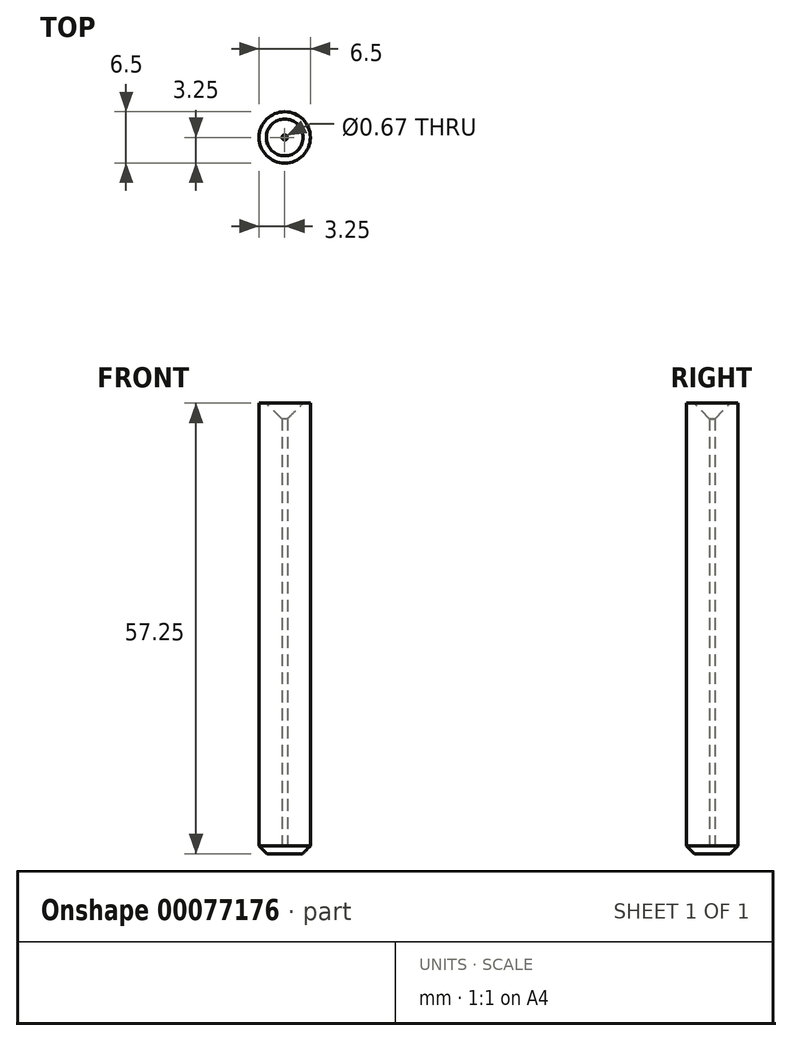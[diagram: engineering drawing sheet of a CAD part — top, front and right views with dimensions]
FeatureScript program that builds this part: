
annotation { "Feature Type Name" : "Feature", "Feature Type Description" : "" }
export const myFeature = defineFeature(function(context is Context, id is Id, definition is map)
    precondition{}
    {
        {
            var Q0;
            Q0=qCreatedBy(makeId("Top.planeOp"),FACE);
            var sketch = newSketch(context, id + "F0", { "sketchPlane" : qUnion([Q0])});
            skCircle(sketch, "E0", {"center": v(0, 0) * mm, "radius": 3.25 * mm});
            skCircle(sketch, "E1", {"center": v(0, 0) * mm, "radius": 0.34 * mm});
            skSolve(sketch);
        }
        {
            var Q0;
            Q0=qSketchRegion(id+"F0",true);
            extrude(context, id + "F1", {"entities" : qUnion([Q0]), "depth" : 57.25 * mm});
        }
        {
            var Q0;
            Q0=makeQuery(id+"F1.opExtrude","CAP_EDGE",EDGE,{"disambiguationData":[OSD([sQuery(id+"F0.wireOp",EDGE,"E1")])],"isStart":false});
            chamfer(context, id + "F2", {"entities" : qUnion([Q0]), "width" : 2 * mm, "tangentPropagation" : true});
        }
        {
            var Q0;
            Q0=makeQuery(id+"F1.opExtrude","CAP_EDGE",EDGE,{"disambiguationData":[OSD([sQuery(id+"F0.wireOp",EDGE,"E0")])],"isStart":true});
            chamfer(context, id + "F3", {"entities" : qUnion([Q0]), "width" : 1 * mm, "tangentPropagation" : true});
        }
    });
